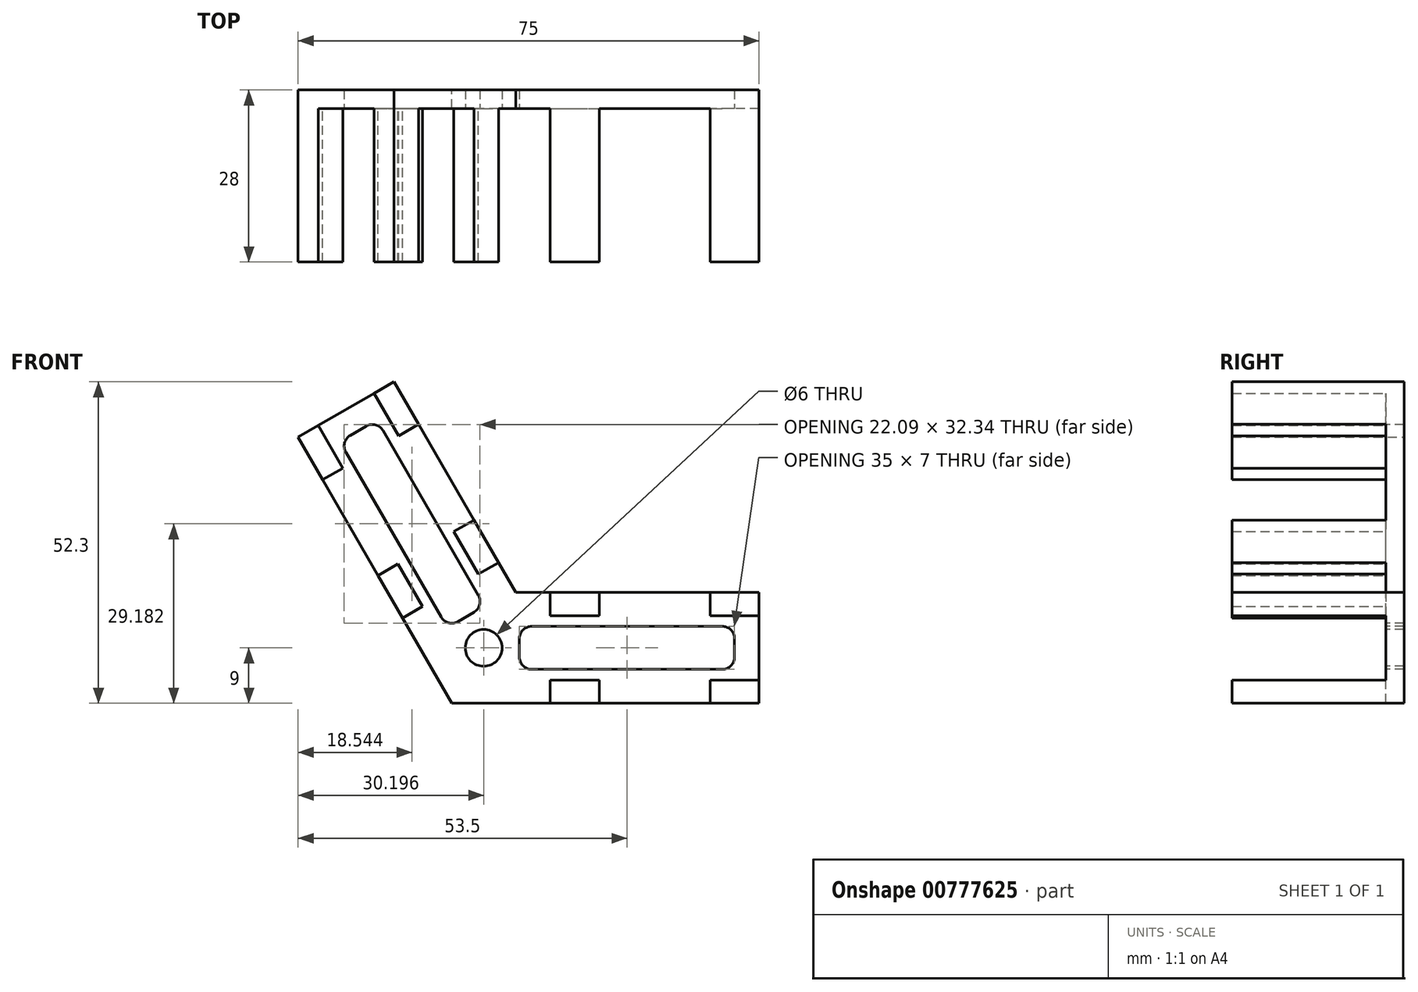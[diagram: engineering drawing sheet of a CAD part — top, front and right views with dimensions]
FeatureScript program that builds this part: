
annotation { "Feature Type Name" : "Feature", "Feature Type Description" : "" }
export const myFeature = defineFeature(function(context is Context, id is Id, definition is map)
    precondition{}
    {
        {
            var Q0;
            Q0=qCreatedBy(makeId("Front.planeOp"),FACE);
            var sketch = newSketch(context, id + "F0", { "sketchPlane" : qUnion([Q0])});
            skLineSegment(sketch, "E0", {"start": v(0, 0) * mm, "end": v(50, 0) * mm});
            skLineSegment(sketch, "E1", {"start": v(10.4, 18) * mm, "end": v(50, 18) * mm});
            skLineSegment(sketch, "E2", {"start": v(50, 18) * mm, "end": v(50, 0) * mm});
            skLineSegment(sketch, "E3", {"start": v(0, 0) * mm, "end": v(-25, 43.3) * mm});
            skLineSegment(sketch, "E4.0", {"start": v(10.4, 18) * mm, "end": v(-9.41, 52.3) * mm});
            skPoint(sketch, "E5.orphan", {"position": v(0, 18) * mm});
            skLineSegment(sketch, "E6", {"start": v(-25, 43.3) * mm, "end": v(-9.41, 52.3) * mm});
            skSolve(sketch);
        }
        {
            var Q0;
            Q0 = qSketchRegion(id + "F0", true);
            extrude(context, id + "F1", {"entities" : qUnion([Q0]), "depth" : 3 * mm, "offsetDistance" : 25 * mm});
        }
        {
            var Q0;
            Q0=makeQuery(id+"F1.opExtrude","CAP_FACE",FACE,{"disambiguationData":[OSD([sQuery(id+"F0.wireOp",EDGE,"E0"),sQuery(id+"F0.wireOp",EDGE,"E1"),sQuery(id+"F0.wireOp",EDGE,"E2"),sQuery(id+"F0.wireOp",EDGE,"E3"),sQuery(id+"F0.wireOp",EDGE,"E4.0"),sQuery(id+"F0.wireOp",EDGE,"E6")])],"isStart":false});
            var sketch = newSketch(context, id + "F2", { "sketchPlane" : qUnion([Q0])});
            skLineSegment(sketch, "E7.bottom", {"start": v(50, 18) * mm, "end": v(42, 18) * mm});
            skLineSegment(sketch, "E7.top", {"start": v(50, 14.25) * mm, "end": v(42, 14.25) * mm});
            skLineSegment(sketch, "E7.left", {"start": v(50, 18) * mm, "end": v(50, 14.25) * mm});
            skLineSegment(sketch, "E7.right", {"start": v(42, 18) * mm, "end": v(42, 14.25) * mm});
            skLineSegment(sketch, "E8.bottom", {"start": v(50, 0) * mm, "end": v(42, 0) * mm});
            skLineSegment(sketch, "E8.top", {"start": v(50, 3.75) * mm, "end": v(42, 3.75) * mm});
            skLineSegment(sketch, "E8.left", {"start": v(50, 0) * mm, "end": v(50, 3.75) * mm});
            skLineSegment(sketch, "E8.right", {"start": v(42, 0) * mm, "end": v(42, 3.75) * mm});
            skLineSegment(sketch, "E9.bottom", {"start": v(16, 18) * mm, "end": v(24, 18) * mm});
            skLineSegment(sketch, "E9.top", {"start": v(16, 14.25) * mm, "end": v(24, 14.25) * mm});
            skLineSegment(sketch, "E9.left", {"start": v(16, 18) * mm, "end": v(16, 14.25) * mm});
            skLineSegment(sketch, "E9.right", {"start": v(24, 18) * mm, "end": v(24, 14.25) * mm});
            skLineSegment(sketch, "E10.bottom", {"start": v(24, 0) * mm, "end": v(16, 0) * mm});
            skLineSegment(sketch, "E10.top", {"start": v(24, 3.75) * mm, "end": v(16, 3.75) * mm});
            skLineSegment(sketch, "E10.left", {"start": v(24, 0) * mm, "end": v(24, 3.75) * mm});
            skLineSegment(sketch, "E10.right", {"start": v(16, 0) * mm, "end": v(16, 3.75) * mm});
            skLineSegment(sketch, "E11", {"start": v(10.4, 18) * mm, "end": v(0, 0) * mm, "construction": true});
            skLineSegment(sketch, "E12.MirrorCS", {"start": v(7.59, 22.86) * mm, "end": v(4.34, 20.98) * mm});
            skLineSegment(sketch, "E13.MirrorCS", {"start": v(3.59, 29.78) * mm, "end": v(0.34, 27.9) * mm});
            skLineSegment(sketch, "E14.MirrorCS", {"start": v(4.34, 20.98) * mm, "end": v(0.34, 27.9) * mm});
            skLineSegment(sketch, "E15.MirrorCS", {"start": v(-8, 13.86) * mm, "end": v(-4.75, 15.73) * mm});
            skLineSegment(sketch, "E16.MirrorCS", {"start": v(-8.75, 22.66) * mm, "end": v(-4.75, 15.73) * mm});
            skLineSegment(sketch, "E17.MirrorCS", {"start": v(-12, 20.78) * mm, "end": v(-8.75, 22.66) * mm});
            skLineSegment(sketch, "E18.MirrorCS", {"start": v(-12, 20.78) * mm, "end": v(-8, 13.86) * mm});
            skLineSegment(sketch, "E19.MirrorCS", {"start": v(7.59, 22.86) * mm, "end": v(3.59, 29.78) * mm});
            skLineSegment(sketch, "E20.MirrorCS", {"start": v(-5.41, 45.37) * mm, "end": v(-8.66, 43.5) * mm});
            skLineSegment(sketch, "E21.MirrorCS", {"start": v(-9.41, 52.3) * mm, "end": v(-5.41, 45.37) * mm});
            skLineSegment(sketch, "E22.MirrorCS", {"start": v(-9.41, 52.3) * mm, "end": v(-12.66, 50.43) * mm});
            skLineSegment(sketch, "E23.MirrorCS", {"start": v(-12.66, 50.43) * mm, "end": v(-8.66, 43.5) * mm});
            skLineSegment(sketch, "E24.MirrorCS", {"start": v(-21.75, 45.18) * mm, "end": v(-17.75, 38.25) * mm});
            skLineSegment(sketch, "E25.MirrorCS", {"start": v(-21, 36.37) * mm, "end": v(-17.75, 38.25) * mm});
            skLineSegment(sketch, "E26.MirrorCS", {"start": v(-25, 43.3) * mm, "end": v(-21.75, 45.18) * mm});
            skLineSegment(sketch, "E27.MirrorCS", {"start": v(-25, 43.3) * mm, "end": v(-21, 36.37) * mm});
            skSolve(sketch);
        }
        {
            var Q0;
            Q0=makeQuery(id+"F2.imprint","IMPRINT",FACE,{"disambiguationData":[TD([[makeQuery(id+"F2.imprint","IMPRINT",EDGE,{"derivedFrom":sQuery(id+"F2.wireOp",EDGE,"E7.bottom")}),-1.0]])]});
            var Q1;
            Q1=makeQuery(id+"F2.imprint","IMPRINT",FACE,{"disambiguationData":[TD([[makeQuery(id+"F2.imprint","IMPRINT",EDGE,{"derivedFrom":sQuery(id+"F2.wireOp",EDGE,"E8.bottom")}),1.0]])]});
            var Q2;
            Q2=makeQuery(id+"F2.imprint","IMPRINT",FACE,{"disambiguationData":[TD([[makeQuery(id+"F2.imprint","IMPRINT",EDGE,{"derivedFrom":sQuery(id+"F2.wireOp",EDGE,"E10.bottom")}),1.0]])]});
            var Q3;
            Q3=makeQuery(id+"F2.imprint","IMPRINT",FACE,{"disambiguationData":[TD([[makeQuery(id+"F2.imprint","IMPRINT",EDGE,{"derivedFrom":sQuery(id+"F2.wireOp",EDGE,"E9.bottom")}),-1.0]])]});
            var Q4;
            Q4=makeQuery(id+"F2.imprint","IMPRINT",FACE,{"disambiguationData":[TD([[makeQuery(id+"F2.imprint","IMPRINT",EDGE,{"derivedFrom":sQuery(id+"F2.wireOp",EDGE,"E12.MirrorCS")}),-1.0]])]});
            var Q5;
            Q5=makeQuery(id+"F2.imprint","IMPRINT",FACE,{"disambiguationData":[TD([[makeQuery(id+"F2.imprint","IMPRINT",EDGE,{"derivedFrom":sQuery(id+"F2.wireOp",EDGE,"E15.MirrorCS")}),1.0]])]});
            var Q6;
            Q6=makeQuery(id+"F2.imprint","IMPRINT",FACE,{"disambiguationData":[TD([[makeQuery(id+"F2.imprint","IMPRINT",EDGE,{"derivedFrom":sQuery(id+"F2.wireOp",EDGE,"E24.MirrorCS")}),-1.0]])]});
            var Q7;
            Q7=makeQuery(id+"F2.imprint","IMPRINT",FACE,{"disambiguationData":[TD([[makeQuery(id+"F2.imprint","IMPRINT",EDGE,{"derivedFrom":sQuery(id+"F2.wireOp",EDGE,"E20.MirrorCS")}),-1.0]])]});
            extrude(context, id + "F3", {"entities" : qUnion([Q0, Q1, Q2, Q3, Q4, Q5, Q6, Q7]), "operationType" : NewBodyOperationType.ADD, "depth" : 25 * mm, "offsetDistance" : 25 * mm});
        }
        {
            var Q0;
            Q0=makeQuery(id+"F1.opExtrude","CAP_FACE",FACE,{"disambiguationData":[OSD([sQuery(id+"F0.wireOp",EDGE,"E0"),sQuery(id+"F0.wireOp",EDGE,"E1"),sQuery(id+"F0.wireOp",EDGE,"E2"),sQuery(id+"F0.wireOp",EDGE,"E3"),sQuery(id+"F0.wireOp",EDGE,"E4.0"),sQuery(id+"F0.wireOp",EDGE,"E6")])],"isStart":false});
            var sketch = newSketch(context, id + "F4", { "sketchPlane" : qUnion([Q0])});
            skLineSegment(sketch, "E28", {"start": v(10.4, 18) * mm, "end": v(0, 0) * mm, "construction": true});
            skLineSegment(sketch, "E29.bottom", {"start": v(13, 12.5) * mm, "end": v(44, 12.5) * mm});
            skLineSegment(sketch, "E29.top", {"start": v(13, 5.5) * mm, "end": v(44, 5.5) * mm});
            skLineSegment(sketch, "E29.left", {"start": v(11, 10.5) * mm, "end": v(11, 7.5) * mm});
            skLineSegment(sketch, "E29.right", {"start": v(46, 10.5) * mm, "end": v(46, 7.5) * mm});
            skLineSegment(sketch, "E30", {"start": v(50, 9) * mm, "end": v(5.2, 9) * mm, "construction": true});
            skPoint(sketch, "E31.visualSharp", {"position": v(46, 12.5) * mm});
            skArc(sketch, "E31.filletArc", {"start": v(46, 10.5) * mm, "mid": v(45.41, 11.91) * mm, "end": v(44, 12.5) * mm});
            skPoint(sketch, "E32.visualSharp", {"position": v(46, 5.5) * mm});
            skArc(sketch, "E32.filletArc", {"start": v(44, 5.5) * mm, "mid": v(45.41, 6.09) * mm, "end": v(46, 7.5) * mm});
            skPoint(sketch, "E33.visualSharp", {"position": v(11, 5.5) * mm});
            skArc(sketch, "E33.filletArc", {"start": v(11, 7.5) * mm, "mid": v(11.59, 6.09) * mm, "end": v(13, 5.5) * mm});
            skPoint(sketch, "E34.visualSharp", {"position": v(11, 12.5) * mm});
            skArc(sketch, "E34.filletArc", {"start": v(13, 12.5) * mm, "mid": v(11.59, 11.91) * mm, "end": v(11, 10.5) * mm});
            skLineSegment(sketch, "E35.MirrorCS", {"start": v(4.33, 17.5) * mm, "end": v(-11.17, 44.36) * mm});
            skArc(sketch, "E36.MirrorCS", {"start": v(-13.9, 45.09) * mm, "mid": v(-12.39, 45.29) * mm, "end": v(-11.17, 44.36) * mm});
            skLineSegment(sketch, "E37.MirrorCS", {"start": v(-13.9, 45.09) * mm, "end": v(-16.5, 43.59) * mm});
            skArc(sketch, "E38.MirrorCS", {"start": v(-17.24, 40.86) * mm, "mid": v(-17.44, 42.37) * mm, "end": v(-16.5, 43.59) * mm});
            skLineSegment(sketch, "E39.MirrorCS", {"start": v(-1.74, 14) * mm, "end": v(-17.24, 40.86) * mm});
            skArc(sketch, "E40.MirrorCS", {"start": v(1, 13.28) * mm, "mid": v(-0.52, 13.08) * mm, "end": v(-1.74, 14) * mm});
            skLineSegment(sketch, "E41.MirrorCS", {"start": v(3.6, 14.78) * mm, "end": v(1, 13.28) * mm});
            skArc(sketch, "E42.MirrorCS", {"start": v(4.33, 17.5) * mm, "mid": v(4.53, 16) * mm, "end": v(3.6, 14.78) * mm});
            skCircle(sketch, "E43", {"center": v(5.2, 9) * mm, "radius": 3 * mm});
            skSolve(sketch);
        }
        {
            var Q0;
            Q0=makeQuery(id+"F4.imprint","IMPRINT",FACE,{"disambiguationData":[TD([[makeQuery(id+"F4.imprint","IMPRINT",EDGE,{"derivedFrom":sQuery(id+"F4.wireOp",EDGE,"E35.MirrorCS")}),1.0]])]});
            var Q1;
            Q1=makeQuery(id+"F4.imprint","IMPRINT",FACE,{"disambiguationData":[TD([[makeQuery(id+"F4.imprint","IMPRINT",EDGE,{"derivedFrom":sQuery(id+"F4.wireOp",EDGE,"E29.bottom")}),-1.0]])]});
            var Q2;
            Q2=makeQuery(id+"F4.imprint","IMPRINT",FACE,{"disambiguationData":[TD([[makeQuery(id+"F4.imprint","IMPRINT",EDGE,{"derivedFrom":sQuery(id+"F4.wireOp",EDGE,"E43")}),1.0]])]});
            extrude(context, id + "F5", {"entities" : qUnion([Q0, Q1, Q2]), "operationType" : NewBodyOperationType.REMOVE, "endBound" : BoundingType.THROUGH_ALL, "oppositeDirection" : true, "depth" : 25 * mm, "offsetDistance" : 25 * mm});
        }
    });
